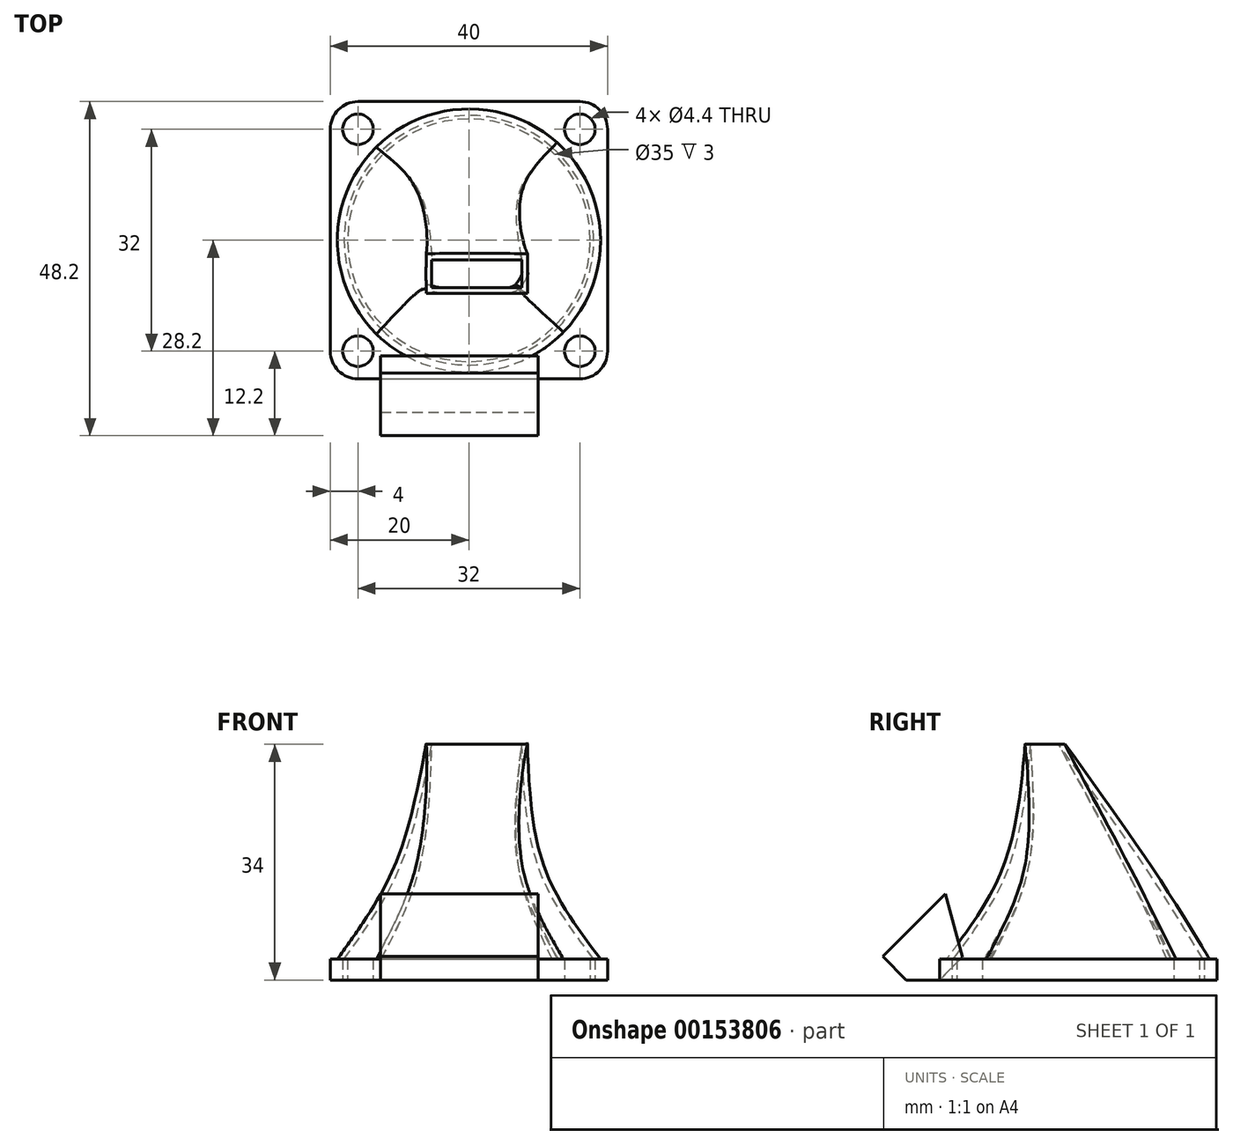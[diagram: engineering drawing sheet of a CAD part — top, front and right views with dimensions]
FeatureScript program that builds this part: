
annotation { "Feature Type Name" : "Feature", "Feature Type Description" : "" }
export const myFeature = defineFeature(function(context is Context, id is Id, definition is map)
    precondition{}
    {
        {
            var Q0;
            Q0=qCreatedBy(makeId("Top.planeOp"),FACE);
            var sketch = newSketch(context, id + "F0", { "sketchPlane" : qUnion([Q0])});
            skLineSegment(sketch, "E0.bottom", {"start": v(-16, 20) * mm, "end": v(16, 20) * mm});
            skLineSegment(sketch, "E0.top", {"start": v(-16, -20) * mm, "end": v(16, -20) * mm});
            skLineSegment(sketch, "E0.left", {"start": v(-20, 16) * mm, "end": v(-20, -16) * mm});
            skLineSegment(sketch, "E0.right", {"start": v(20, 16) * mm, "end": v(20, -16) * mm});
            skPoint(sketch, "E0.middle", {"position": v(0, 0) * mm});
            skPoint(sketch, "E1.visualSharp", {"position": v(-20, 20) * mm});
            skArc(sketch, "E1.filletArc", {"start": v(-16, 20) * mm, "mid": v(-18.83, 18.83) * mm, "end": v(-20, 16) * mm});
            skPoint(sketch, "E2.visualSharp", {"position": v(20, 20) * mm});
            skArc(sketch, "E2.filletArc", {"start": v(20, 16) * mm, "mid": v(18.83, 18.83) * mm, "end": v(16, 20) * mm});
            skPoint(sketch, "E3.visualSharp", {"position": v(-20, -20) * mm});
            skArc(sketch, "E3.filletArc", {"start": v(-20, -16) * mm, "mid": v(-18.83, -18.83) * mm, "end": v(-16, -20) * mm});
            skPoint(sketch, "E4.visualSharp", {"position": v(20, -20) * mm});
            skArc(sketch, "E4.filletArc", {"start": v(16, -20) * mm, "mid": v(18.83, -18.83) * mm, "end": v(20, -16) * mm});
            skCircle(sketch, "E5", {"center": v(-16, 16) * mm, "radius": 2.2 * mm});
            skCircle(sketch, "E6", {"center": v(16, 16) * mm, "radius": 2.2 * mm});
            skCircle(sketch, "E7", {"center": v(-16, -16) * mm, "radius": 2.2 * mm});
            skCircle(sketch, "E8", {"center": v(16, -16) * mm, "radius": 2.2 * mm});
            skCircle(sketch, "E9", {"center": v(0, 0) * mm, "radius": 17.5 * mm});
            skSolve(sketch);
        }
        {
            var Q0;
            Q0 = qSketchRegion(id + "F0", true);
            extrude(context, id + "F1", {"entities" : qUnion([Q0]), "depth" : 3 * mm});
        }
        {
            var Q0;
            Q0=makeQuery(id+"F1.opExtrude","CAP_FACE",FACE,{"disambiguationData":[OSD([sQuery(id+"F0.wireOp",EDGE,"E0.bottom"),sQuery(id+"F0.wireOp",EDGE,"E0.top"),sQuery(id+"F0.wireOp",EDGE,"E0.left"),sQuery(id+"F0.wireOp",EDGE,"E0.right"),sQuery(id+"F0.wireOp",EDGE,"E1.filletArc"),sQuery(id+"F0.wireOp",EDGE,"E2.filletArc"),sQuery(id+"F0.wireOp",EDGE,"E3.filletArc"),sQuery(id+"F0.wireOp",EDGE,"E4.filletArc"),sQuery(id+"F0.wireOp",EDGE,"E5"),sQuery(id+"F0.wireOp",EDGE,"E6"),sQuery(id+"F0.wireOp",EDGE,"E7"),sQuery(id+"F0.wireOp",EDGE,"E8"),sQuery(id+"F0.wireOp",EDGE,"E9")])],"isStart":false});
            cPlane(context, id + "F2", {"entities" : qUnion([Q0]), "cplaneType" : CPlaneType.OFFSET, "offset" : 0 * mm, "width" : 150 * mm, "height" : 150 * mm});
        }
        {
            var Q0;
            Q0=qCreatedBy(id+"F2.planeOp",FACE);
            var sketch = newSketch(context, id + "F3", { "sketchPlane" : qUnion([Q0])});
            skArc(sketch, "E10", {"start": v(-12.64, -12.81) * mm, "mid": v(0.18, -18) * mm, "end": v(12.9, -12.56) * mm});
            skArc(sketch, "E11", {"start": v(12.9, -12.56) * mm, "mid": v(18, 0.59) * mm, "end": v(12.04, 13.38) * mm});
            skArc(sketch, "E12", {"start": v(12.04, 13.38) * mm, "mid": v(-0.44, 18) * mm, "end": v(-12.68, 12.78) * mm});
            skArc(sketch, "E13", {"start": v(-12.68, 12.78) * mm, "mid": v(-18, -0.03) * mm, "end": v(-12.64, -12.81) * mm});
            skSolve(sketch);
        }
        {
            var Q0;
            Q0=qCreatedBy(makeId("Top.planeOp"),FACE);
            cPlane(context, id + "F4", {"entities" : qUnion([Q0]), "cplaneType" : CPlaneType.OFFSET, "offset" : 15 * mm, "width" : 150 * mm, "height" : 150 * mm});
        }
        {
            var Q0;
            Q0=qCreatedBy(id+"F4.planeOp",FACE);
            var sketch = newSketch(context, id + "F5", { "sketchPlane" : qUnion([Q0])});
            skLineSegment(sketch, "E14", {"start": v(0, 0) * mm, "end": v(7.42, 7.42) * mm, "construction": true});
            skArc(sketch, "E15", {"start": v(7.42, 7.42) * mm, "mid": v(0, 10.5) * mm, "end": v(-7.42, 7.42) * mm});
            skArc(sketch, "E16", {"start": v(-7.42, 7.42) * mm, "mid": v(-10.5, 0) * mm, "end": v(-7.42, -7.42) * mm});
            skArc(sketch, "E17", {"start": v(-7.42, -7.42) * mm, "mid": v(0, -10.5) * mm, "end": v(7.42, -7.42) * mm});
            skArc(sketch, "E18", {"start": v(7.42, -7.42) * mm, "mid": v(10.5, 0) * mm, "end": v(7.42, 7.42) * mm});
            skSolve(sketch);
        }
        {
            var Q0;
            Q0=qCreatedBy(makeId("Top.planeOp"),FACE);
            cPlane(context, id + "F6", {"entities" : qUnion([Q0]), "cplaneType" : CPlaneType.OFFSET, "offset" : 34 * mm, "width" : 150 * mm, "height" : 150 * mm});
        }
        {
            var Q0;
            Q0=qCreatedBy(id+"F6.planeOp",FACE);
            var sketch = newSketch(context, id + "F7", { "sketchPlane" : qUnion([Q0])});
            skLineSegment(sketch, "E19.bottom", {"start": v(7.63, -2.85) * mm, "end": v(-5.37, -2.85) * mm});
            skLineSegment(sketch, "E19.top", {"start": v(7.63, -6.85) * mm, "end": v(-5.37, -6.85) * mm});
            skLineSegment(sketch, "E19.left", {"start": v(7.63, -2.85) * mm, "end": v(7.63, -6.85) * mm});
            skLineSegment(sketch, "E19.right", {"start": v(-5.37, -2.85) * mm, "end": v(-5.37, -6.85) * mm});
            skPoint(sketch, "E20.visualSharp", {"position": v(-5.37, -2.85) * mm});
            skPoint(sketch, "E21.visualSharp", {"position": v(7.63, -2.85) * mm});
            skPoint(sketch, "E22.visualSharp", {"position": v(7.63, -6.85) * mm});
            skPoint(sketch, "E23.visualSharp", {"position": v(-5.35, 3.53) * mm});
            skSolve(sketch);
        }
        {
            var Q0;
            Q0 = qSketchRegion(id + "F3", true);
            var Q1;
            Q1 = qSketchRegion(id + "F5", true);
            var Q2;
            Q2 = qSketchRegion(id + "F7", true);
            loft(context, id + "F8", {"sheetProfilesArray" : [{ "sheetProfileEntities" : qUnion([Q0]) }, { "sheetProfileEntities" : qUnion([Q1]) }, { "sheetProfileEntities" : qUnion([Q2]) }]});
        }
        {
            var Q0;
            Q0=makeQuery(id+"F8.opLoft","CAP_FACE",FACE,{"disambiguationData":[OSD([makeQuery(id+"F7.imprint","IMPRINT",FACE,{"disambiguationData":[TD([[makeQuery(id+"F7.imprint","IMPRINT",EDGE,{"derivedFrom":sQuery(id+"F7.wireOp",EDGE,"E19.bottom")}),1.0]])]})])],"isStart":true});
            var Q1;
            Q1=makeQuery(id+"F8.opLoft","CAP_FACE",FACE,{"disambiguationData":[OSD([makeQuery(id+"F3.imprint","IMPRINT",FACE,{"disambiguationData":[TD([[makeQuery(id+"F3.imprint","IMPRINT",EDGE,{"derivedFrom":sQuery(id+"F3.wireOp",EDGE,"E10")}),1.0]])]})])],"isStart":true});
            shell(context, id + "F9", {"entities" : qUnion([Q0, Q1]), "thickness" : 0.8 * mm, "oppositeDirection" : true});
        }
        {
            var Q0;
            Q0=qCreatedBy(makeId("Right.planeOp"),FACE);
            cPlane(context, id + "F10", {"entities" : qUnion([Q0]), "cplaneType" : CPlaneType.OFFSET, "offset" : 10 * mm, "width" : 150 * mm, "height" : 150 * mm});
        }
        {
            var Q0;
            Q0=qCreatedBy(id+"F10.planeOp",FACE);
            var sketch = newSketch(context, id + "F11", { "sketchPlane" : qUnion([Q0])});
            skLineSegment(sketch, "E24.1", {"start": v(-19.15, 12.45) * mm, "end": v(-16.7, 3.3) * mm});
            skLineSegment(sketch, "E24.3", {"start": v(-24.8, 0) * mm, "end": v(-28.2, 3.4) * mm});
            skLineSegment(sketch, "E25", {"start": v(-24.8, 0) * mm, "end": v(-20, 0) * mm});
            skLineSegment(sketch, "E26.0", {"start": v(-28.2, 3.4) * mm, "end": v(-19.15, 12.45) * mm});
            skLineSegment(sketch, "E27", {"start": v(-16.7, 3.3) * mm, "end": v(-20, 0) * mm});
            skSolve(sketch);
        }
        {
            var Q0;
            Q0 = qSketchRegion(id + "F11", true);
            extrude(context, id + "F12", {"entities" : qUnion([Q0]), "oppositeDirection" : true, "depth" : 22.75 * mm});
        }
        {
            var Q0;
            Q0=makeQuery(id+"F1.opExtrude","CAP_FACE",FACE,{"disambiguationData":[OSD([sQuery(id+"F0.wireOp",EDGE,"E0.bottom"),sQuery(id+"F0.wireOp",EDGE,"E0.top"),sQuery(id+"F0.wireOp",EDGE,"E0.left"),sQuery(id+"F0.wireOp",EDGE,"E0.right"),sQuery(id+"F0.wireOp",EDGE,"E1.filletArc"),sQuery(id+"F0.wireOp",EDGE,"E2.filletArc"),sQuery(id+"F0.wireOp",EDGE,"E3.filletArc"),sQuery(id+"F0.wireOp",EDGE,"E4.filletArc"),sQuery(id+"F0.wireOp",EDGE,"E5"),sQuery(id+"F0.wireOp",EDGE,"E6"),sQuery(id+"F0.wireOp",EDGE,"E7"),sQuery(id+"F0.wireOp",EDGE,"E8"),sQuery(id+"F0.wireOp",EDGE,"E9")])],"isStart":true});
            var sketch = newSketch(context, id + "F13", { "sketchPlane" : qUnion([Q0])});
            skCircle(sketch, "E28", {"center": v(-16, 16) * mm, "radius": 2.2 * mm});
            skCircle(sketch, "E29", {"center": v(16, 16) * mm, "radius": 2.2 * mm});
            skSolve(sketch);
        }
        {
            var Q0;
            Q0 = qSketchRegion(id + "F13", true);
            extrude(context, id + "F14", {"entities" : qUnion([Q0]), "operationType" : NewBodyOperationType.REMOVE, "endBound" : BoundingType.THROUGH_ALL, "oppositeDirection" : true, "depth" : 25 * mm});
        }
    });
